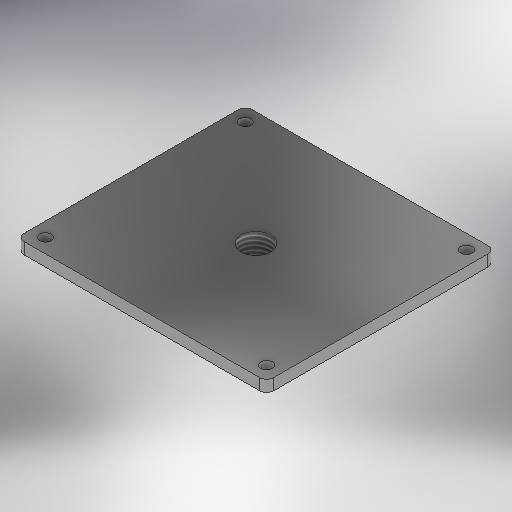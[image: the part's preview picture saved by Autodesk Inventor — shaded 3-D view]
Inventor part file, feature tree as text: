
AUTODESK INVENTOR PART (.ipt)
format: ipt  version: 2025 (Build 290162000, 162)  size: 371,200 bytes
history: native  units: mm
features: sketch x5, extrude x3, fillet x2, hole x1
ambient origin geometry x8: Origin, YZ Plane, XZ Plane, XY Plane, X Axis, Y Axis, Z Axis, Center Point
bodies: 实体1 (feature_tree)
feature tree (11):
  sketch  "草图1"  dims[d4=8.0mm d0=160.0mm]
  extrude  "拉伸1"  Depth=160.0mm
  extrude  "拉伸2"  Depth=8.0mm
  fillet  "圆角1"  Radius=20.0mm
  extrude  "拉伸3"  Depth=5.0mm
  fillet  "圆角2"  Radius=8.0mm
  hole  "孔2"  [1 undecoded]
  sketch  "草图 - 矩形阵列1"  dims[d1=175.0mm d2=8.0mm d3=20.0mm d6=140.0mm]
  sketch  "草图2"  dims[d7=20.0mm d9=155.0mm d12=5.0mm d13=8.0mm]
  sketch  "草图3"  dims[d14=0.0mm d15=5.0mm]
  sketch  "草图4"  dims[d16=120.0mm d17=135.0mm d18=1.5mm d19=0.0mm d20=2.0mm d28=32.0mm d29=8.5mm d30=0.0mm d31=2.0mm d32=20.752mm d33=48.0mm d34=4.0mm d35=2.0mm d36=90.0deg d37=8.0mm d38=120.0deg]
note: 1 required parameter value undecoded (feature->parameter linkage not recoverable at this tier; creation-order binding heuristic only, values carry confidence <= 0.55)
